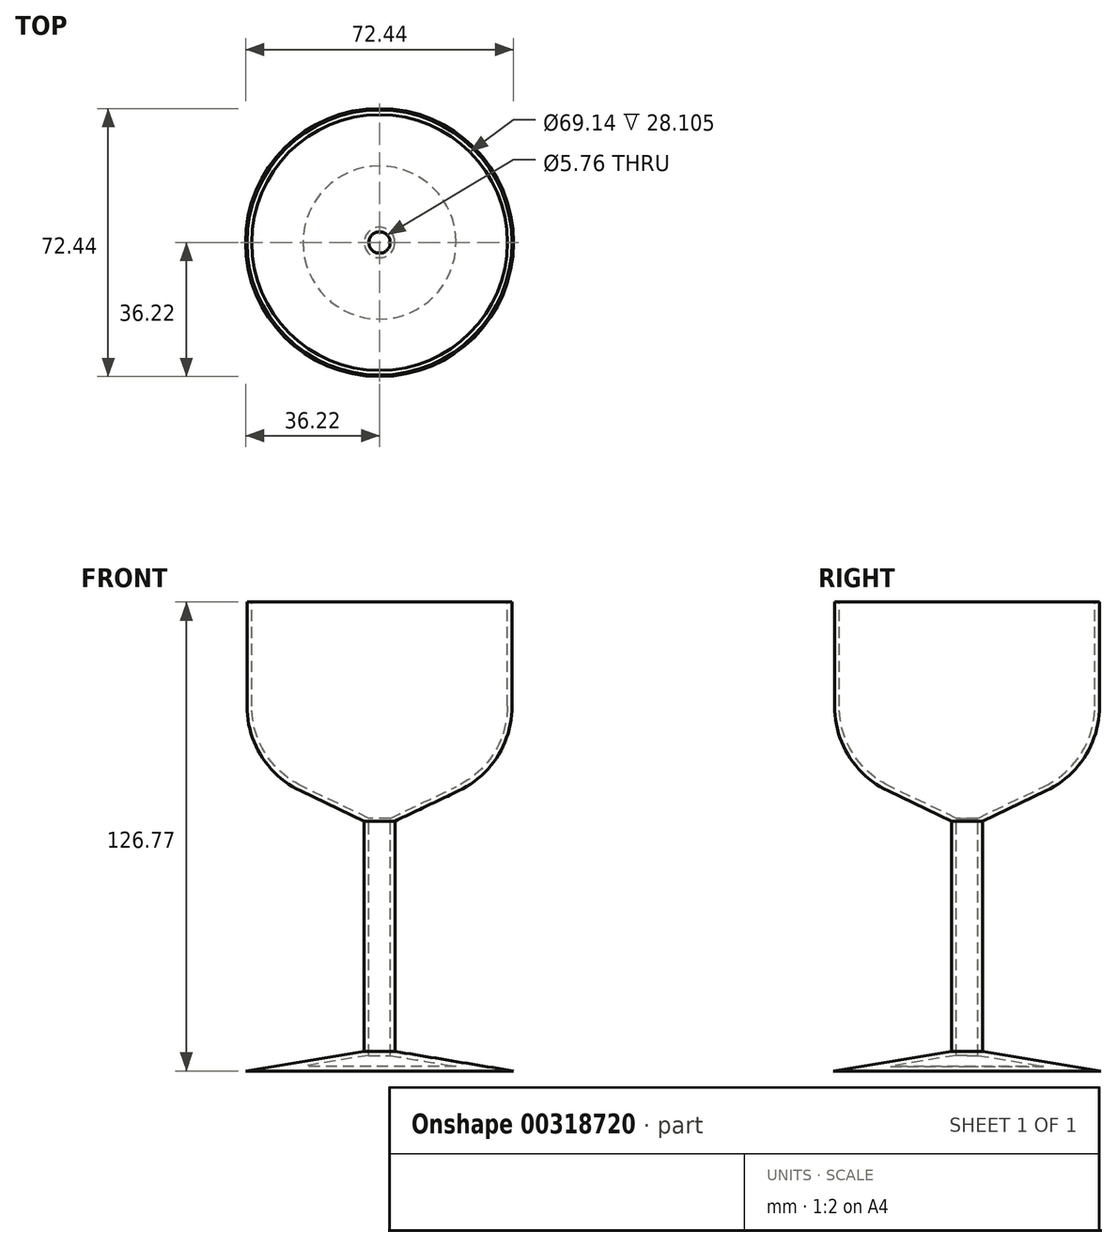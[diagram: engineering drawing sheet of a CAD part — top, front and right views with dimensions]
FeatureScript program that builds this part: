
annotation { "Feature Type Name" : "Feature", "Feature Type Description" : "" }
export const myFeature = defineFeature(function(context is Context, id is Id, definition is map)
    precondition{}
    {
        {
            var Q0;
            Q0=qCreatedBy(makeId("Front.planeOp"),FACE);
            var sketch = newSketch(context, id + "F0", { "sketchPlane" : qUnion([Q0])});
            skLineSegment(sketch, "E0", {"start": v(0, -76.4) * mm, "end": v(-36.22, -76.4) * mm});
            skLineSegment(sketch, "E1", {"start": v(-36.22, -76.4) * mm, "end": v(-4.15, -71.12) * mm});
            skLineSegment(sketch, "E2", {"start": v(-4.15, -71.12) * mm, "end": v(-4.15, -8.87) * mm});
            skLineSegment(sketch, "E3", {"start": v(-4.15, -8.87) * mm, "end": v(-35.84, 6.23) * mm});
            skLineSegment(sketch, "E4", {"start": v(-35.84, 6.23) * mm, "end": v(-35.84, 50.37) * mm});
            skLineSegment(sketch, "E5", {"start": v(-35.84, 50.37) * mm, "end": v(0, 50.37) * mm});
            skLineSegment(sketch, "E6", {"start": v(0, 50.37) * mm, "end": v(0, -76.4) * mm});
            skSolve(sketch);
        }
        {
            var Q0;
            Q0=makeQuery(id+"F0.imprint","IMPRINT",FACE,{"disambiguationData":[TD([[makeQuery(id+"F0.imprint","IMPRINT",EDGE,{"derivedFrom":sQuery(id+"F0.wireOp",EDGE,"E0")}),-1.0]])]});
            var Q1;
            Q1=sQuery(id+"F0.wireOp",EDGE,"E6");
            revolve(context, id + "F1", {"entities" : qUnion([Q0]), "axis" : qUnion([Q1]), "revolveType" : RevolveType.FULL});
        }
        {
            var Q0;
            Q0=makeQuery(id+"F1.opRevolve","SWEPT_EDGE",EDGE,{"disambiguationData":[OSD([sQuery(id+"F0.wireOp",EDGE,"E3"),sQuery(id+"F0.wireOp",EDGE,"E4")])]});
            fillet(context, id + "F2", {"entities" : qUnion([Q0]), "radius" : 25.4 * mm, "tangentPropagation" : true, "allowEdgeOverflow" : false});
        }
        {
            var Q0;
            Q0=makeQuery(id+"F1.opRevolve","SWEPT_FACE",FACE,{"disambiguationData":[OSD([sQuery(id+"F0.wireOp",EDGE,"E5")])]});
            shell(context, id + "F3", {"entities" : qUnion([Q0]), "thickness" : 1.27 * mm});
        }
    });
